# Revit family: Fixture_Support_Water_Closet_Offset_Horizontal-Zurn-Z1201-ND3-FMBO
name_source: partatom
category: Plumbing Fixtures
units: mm (PartAtom-declared; Revit-internal decimal feet)

## family parameters
Always vertical = Yes
Cut with Voids When Loaded = No
Maintain Annotation Orientation = No
OmniClass Number = 23.45.55.11
OmniClass Title = Sanitary Components
Part Type = Normal
Room Calculation Point = No
Round Connector Dimension = Use Radius
Shared = No
Work Plane-Based = No

## types (1)
- Z1201-ND3-FMBO
    Approx.Weight = 63.00 lb
    Assembly Code = D2030400
    CW Connection = No
    CWFU = 0
    Connector sketch = No
    Coupling = ABS - Zurn - Plastic
    Default Elevation = 25 "
    Description = EZCARRY® ADJUSTABLE HORIZONTAL HIGH PERFORMANCE BACK-TO-BACK SIPHON JET NO-HUB WATER CLOSET CARRIER SYSTEM W/ FLOOR MOUNTED, BACK OUTLET FIXTURE SUPPORT
    Diameter of Coupling_K = 4.625 "
    Dimension (N) = 11.25 "
    Dimesion (B) = 11.5 "
    HW Connection = No
    HWFU = 0
    Hardware = Steel - Zurn  - Galvanized
    Inlet/Outlet Actual Radius = 1.75 "
    Inlet/Outlet Inner Radius = 1.534 "
    Inlet/Outlet Nominal Radius = 1.5 "
    Main Material = Iron - Zurn - Cast - Painted - Blue
    Manufacturer = Zurn Water, LLC
    Manufacurer Brand = Zurn
    Model = Z1201-ND3-FMBO
    Modified Date = 01/23/2026
    Product Documentation Link = https://files.zurn.com
    Product Installation Sheet URL = https://files.zurn.com
    Product Page URL = https://www.zurn.com
    Product data url = https://www.bimobject.com
    URL = www.zurn.com
    Vent Actual radius = 1.188 "
    Vent Connection = Yes
    Vent Inner radius = 1.034 "
    Vent Nominal radius = 1 "
    WFU = 1
    Waste Connection = Yes

## geometry (parser evidence)
native form markers: Sweep x10
no freeform markers — native parametric forms only
